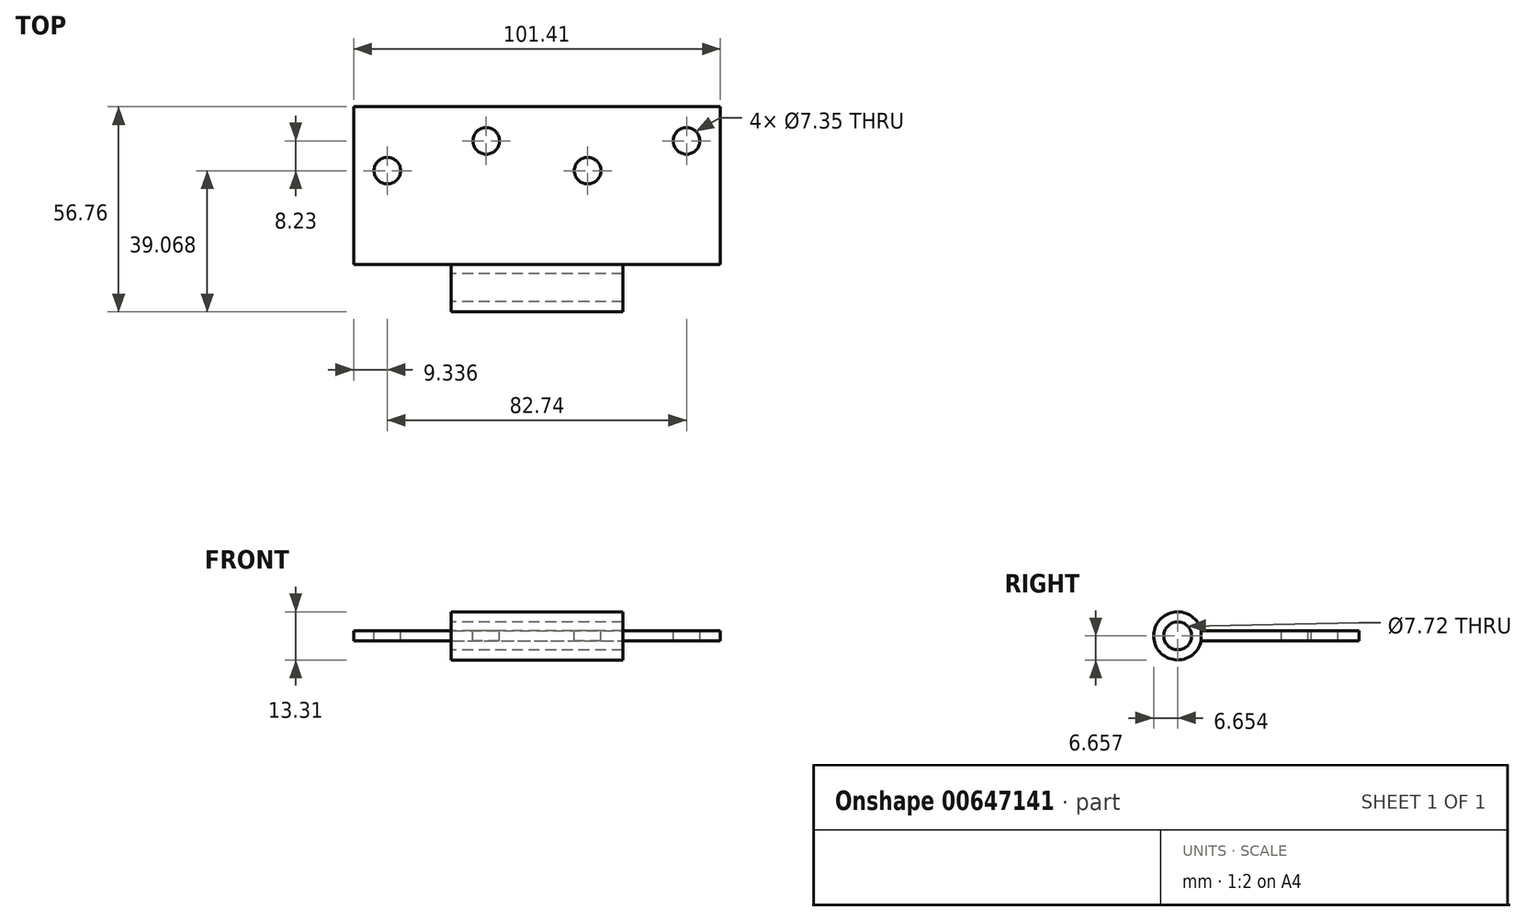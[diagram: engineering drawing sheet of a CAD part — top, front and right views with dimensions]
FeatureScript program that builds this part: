
annotation { "Feature Type Name" : "Feature", "Feature Type Description" : "" }
export const myFeature = defineFeature(function(context is Context, id is Id, definition is map)
    precondition{}
    {
        {
            var Q0;
            Q0=qCreatedBy(makeId("Top.planeOp"),FACE);
            var sketch = newSketch(context, id + "F0", { "sketchPlane" : qUnion([Q0])});
            skLineSegment(sketch, "E0.bottom", {"start": v(-50.7, 21.8) * mm, "end": v(50.71, 21.8) * mm});
            skLineSegment(sketch, "E0.top", {"start": v(-50.7, -21.8) * mm, "end": v(50.71, -21.8) * mm});
            skLineSegment(sketch, "E0.left", {"start": v(-50.7, 21.8) * mm, "end": v(-50.7, -21.8) * mm});
            skLineSegment(sketch, "E0.right", {"start": v(50.71, 21.8) * mm, "end": v(50.71, -21.8) * mm});
            skSolve(sketch);
        }
        {
            var Q0;
            Q0 = qSketchRegion(id + "F0", true);
            extrude(context, id + "F1", {"entities" : qUnion([Q0]), "depth" : 2.8 * mm, "offsetDistance" : 25.4 * mm});
        }
        {
            var Q0;
            Q0=qCreatedBy(makeId("Right.planeOp"),FACE);
            var sketch = newSketch(context, id + "F2", { "sketchPlane" : qUnion([Q0])});
            skCircle(sketch, "E1", {"center": v(-28.3, 1.4) * mm, "radius": 6.65 * mm});
            skPoint(sketch, "E2", {"position": v(-21.8, 1.4) * mm});
            skCircle(sketch, "E3.0", {"center": v(-28.3, 1.4) * mm, "radius": 3.86 * mm});
            skSolve(sketch);
        }
        {
            var Q0;
            Q0 = qSketchRegion(id + "F2", true);
            extrude(context, id + "F3", {"entities" : qUnion([Q0]), "operationType" : NewBodyOperationType.ADD, "depth" : 23.72 * mm, "offsetDistance" : 25.4 * mm, "hasSecondDirection" : true, "secondDirectionOppositeDirection" : true, "secondDirectionDepth" : 23.72 * mm});
        }
        {
            var Q0;
            Q0=makeQuery(id+"F1.opExtrude","CAP_FACE",FACE,{"disambiguationData":[OSD([sQuery(id+"F0.wireOp",EDGE,"E0.bottom"),sQuery(id+"F0.wireOp",EDGE,"E0.top"),sQuery(id+"F0.wireOp",EDGE,"E0.left"),sQuery(id+"F0.wireOp",EDGE,"E0.right")])],"isStart":false});
            var sketch = newSketch(context, id + "F4", { "sketchPlane" : qUnion([Q0])});
            skPoint(sketch, "E4", {"position": v(41.38, 12.34) * mm});
            skPoint(sketch, "E5", {"position": v(-14, 12.34) * mm});
            skPoint(sketch, "E6", {"position": v(14.02, 4.1) * mm});
            skPoint(sketch, "E7", {"position": v(-41.36, 4.1) * mm});
            skSolve(sketch);
        }
        {
            var Q0;
            Q0=sQuery(id+"F4.wireOp",VERTEX,"E6");
            var Q1;
            Q1=sQuery(id+"F4.wireOp",VERTEX,"E5");
            var Q2;
            Q2=sQuery(id+"F4.wireOp",VERTEX,"E7");
            var Q3;
            Q3=sQuery(id+"F4.wireOp",VERTEX,"E4");
            var Q4;
            Q4=makeQuery(id+"F1.opExtrude","SWEPT_BODY",BODY,{"disambiguationData":[OSD([sQuery(id+"F0.wireOp",EDGE,"E0.bottom"),sQuery(id+"F0.wireOp",EDGE,"E0.top"),sQuery(id+"F0.wireOp",EDGE,"E0.left"),sQuery(id+"F0.wireOp",EDGE,"E0.right")])]});
            hole(context, id + "F5", {"style" : HoleStyle.SIMPLE, "endStyle" : HoleEndStyle.BLIND, "holeDiameter" : 7.35 * mm, "majorDiameter" : 6.35 * mm, "holeDepth" : 12.7 * mm, "isTappedThrough" : true, "tappedDepth" : 12.7 * mm, "tapClearance" : 3, "locations" : qUnion([Q0, Q1, Q2, Q3]), "scope" : qUnion([Q4])});
        }
    });
